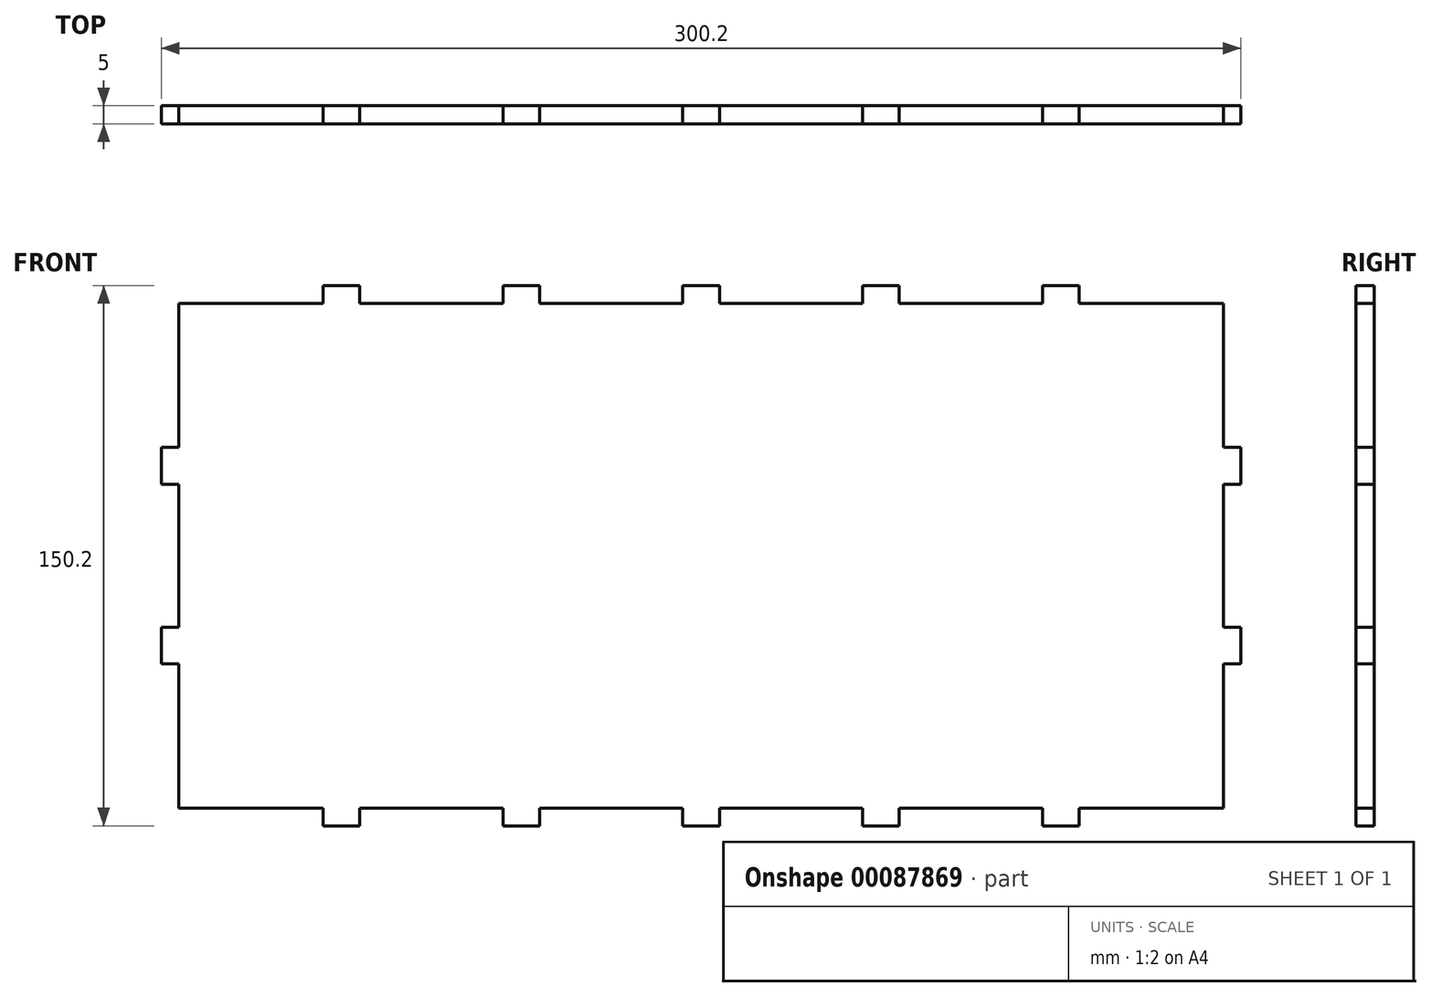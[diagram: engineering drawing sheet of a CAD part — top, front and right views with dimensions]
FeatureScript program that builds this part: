
annotation { "Feature Type Name" : "Feature", "Feature Type Description" : "" }
export const myFeature = defineFeature(function(context is Context, id is Id, definition is map)
    precondition{}
    {
        {
            var Q0;
            Q0=qCreatedBy(makeId("Front.planeOp"),FACE);
            var sketch = newSketch(context, id + "F0", { "sketchPlane" : qUnion([Q0])});
            skLineSegment(sketch, "E0.bottom", {"start": v(150.1, 75.1) * mm, "end": v(-150.1, 75.1) * mm});
            skLineSegment(sketch, "E0.top", {"start": v(150.1, -75.1) * mm, "end": v(-150.1, -75.1) * mm});
            skLineSegment(sketch, "E0.left", {"start": v(150.1, 75.1) * mm, "end": v(150.1, -75.1) * mm});
            skLineSegment(sketch, "E0.right", {"start": v(-150.1, 75.1) * mm, "end": v(-150.1, -75.1) * mm});
            skPoint(sketch, "E0.middle", {"position": v(0, 0) * mm});
            skSolve(sketch);
        }
        {
            var Q0;
            Q0=makeQuery(id+"F0.imprint","IMPRINT",FACE,{"disambiguationData":[TD([[makeQuery(id+"F0.imprint","IMPRINT",EDGE,{"derivedFrom":sQuery(id+"F0.wireOp",EDGE,"E0.bottom")}),1.0]])]});
            extrude(context, id + "F1", {"entities" : qUnion([Q0]), "depth" : 5 * mm});
        }
        {
            var Q0;
            Q0=makeQuery(id+"F1.opExtrude","CAP_FACE",FACE,{"disambiguationData":[OSD([sQuery(id+"F0.wireOp",EDGE,"E0.bottom"),sQuery(id+"F0.wireOp",EDGE,"E0.top"),sQuery(id+"F0.wireOp",EDGE,"E0.left"),sQuery(id+"F0.wireOp",EDGE,"E0.right")])],"isStart":false});
            var sketch = newSketch(context, id + "F2", { "sketchPlane" : qUnion([Q0])});
            skLineSegment(sketch, "E1.bottom", {"start": v(-150.1, 75.1) * mm, "end": v(-145.2, 75.1) * mm});
            skLineSegment(sketch, "E1.top", {"start": v(-150.1, 30.1) * mm, "end": v(-145.2, 30.1) * mm});
            skLineSegment(sketch, "E1.left", {"start": v(-150.1, 75.1) * mm, "end": v(-150.1, 30.1) * mm});
            skLineSegment(sketch, "E1.right", {"start": v(-145.2, 75.1) * mm, "end": v(-145.2, 30.1) * mm});
            skLineSegment(sketch, "E2.bottom", {"start": v(-150.1, 19.9) * mm, "end": v(-145.2, 19.9) * mm});
            skLineSegment(sketch, "E2.top", {"start": v(-150.1, -19.9) * mm, "end": v(-145.2, -19.9) * mm});
            skLineSegment(sketch, "E2.left", {"start": v(-150.1, 19.9) * mm, "end": v(-150.1, -19.9) * mm});
            skLineSegment(sketch, "E2.right", {"start": v(-145.2, 19.9) * mm, "end": v(-145.2, -19.9) * mm});
            skLineSegment(sketch, "E3.bottom", {"start": v(-150.1, -30.1) * mm, "end": v(-145.2, -30.1) * mm});
            skLineSegment(sketch, "E3.top", {"start": v(-150.1, -75.1) * mm, "end": v(-145.2, -75.1) * mm});
            skLineSegment(sketch, "E3.left", {"start": v(-150.1, -30.1) * mm, "end": v(-150.1, -75.1) * mm});
            skLineSegment(sketch, "E3.right", {"start": v(-145.2, -30.1) * mm, "end": v(-145.2, -75.1) * mm});
            skLineSegment(sketch, "E4.bottom", {"start": v(-150.1, 75.1) * mm, "end": v(-105.1, 75.1) * mm});
            skLineSegment(sketch, "E4.top", {"start": v(-150.1, 70.2) * mm, "end": v(-105.1, 70.2) * mm});
            skLineSegment(sketch, "E4.left", {"start": v(-150.1, 75.1) * mm, "end": v(-150.1, 70.2) * mm});
            skLineSegment(sketch, "E4.right", {"start": v(-105.1, 75.1) * mm, "end": v(-105.1, 70.2) * mm});
            skLineSegment(sketch, "E5.bottom", {"start": v(-94.9, 75.1) * mm, "end": v(-55.1, 75.1) * mm});
            skLineSegment(sketch, "E5.top", {"start": v(-94.9, 70.2) * mm, "end": v(-55.1, 70.2) * mm});
            skLineSegment(sketch, "E5.left", {"start": v(-94.9, 75.1) * mm, "end": v(-94.9, 70.2) * mm});
            skLineSegment(sketch, "E5.right", {"start": v(-55.1, 75.1) * mm, "end": v(-55.1, 70.2) * mm});
            skLineSegment(sketch, "E6.bottom", {"start": v(-44.9, 75.1) * mm, "end": v(-5.1, 75.1) * mm});
            skLineSegment(sketch, "E6.top", {"start": v(-44.9, 70.2) * mm, "end": v(-5.1, 70.2) * mm});
            skLineSegment(sketch, "E6.left", {"start": v(-44.9, 75.1) * mm, "end": v(-44.9, 70.2) * mm});
            skLineSegment(sketch, "E6.right", {"start": v(-5.1, 75.1) * mm, "end": v(-5.1, 70.2) * mm});
            skLineSegment(sketch, "E7.bottom", {"start": v(5.1, 75.1) * mm, "end": v(44.9, 75.1) * mm});
            skLineSegment(sketch, "E7.top", {"start": v(5.1, 70.2) * mm, "end": v(44.9, 70.2) * mm});
            skLineSegment(sketch, "E7.left", {"start": v(5.1, 75.1) * mm, "end": v(5.1, 70.2) * mm});
            skLineSegment(sketch, "E7.right", {"start": v(44.9, 75.1) * mm, "end": v(44.9, 70.2) * mm});
            skLineSegment(sketch, "E8.bottom", {"start": v(55.1, 75.1) * mm, "end": v(94.9, 75.1) * mm});
            skLineSegment(sketch, "E8.top", {"start": v(55.1, 70.2) * mm, "end": v(94.9, 70.2) * mm});
            skLineSegment(sketch, "E8.left", {"start": v(55.1, 75.1) * mm, "end": v(55.1, 70.2) * mm});
            skLineSegment(sketch, "E8.right", {"start": v(94.9, 75.1) * mm, "end": v(94.9, 70.2) * mm});
            skLineSegment(sketch, "E9.bottom", {"start": v(150.1, 75.1) * mm, "end": v(105.1, 75.1) * mm});
            skLineSegment(sketch, "E9.top", {"start": v(150.1, 70.2) * mm, "end": v(105.1, 70.2) * mm});
            skLineSegment(sketch, "E9.left", {"start": v(150.1, 75.1) * mm, "end": v(150.1, 70.2) * mm});
            skLineSegment(sketch, "E9.right", {"start": v(105.1, 75.1) * mm, "end": v(105.1, 70.2) * mm});
            skLineSegment(sketch, "E10.MirrorCS", {"start": v(-150.1, -75.1) * mm, "end": v(-150.1, -70.2) * mm});
            skLineSegment(sketch, "E11.MirrorCS", {"start": v(44.9, -75.1) * mm, "end": v(44.9, -70.2) * mm});
            skLineSegment(sketch, "E12.MirrorCS", {"start": v(-5.1, -75.1) * mm, "end": v(-5.1, -70.2) * mm});
            skLineSegment(sketch, "E13.MirrorCS", {"start": v(-55.1, -75.1) * mm, "end": v(-55.1, -70.2) * mm});
            skLineSegment(sketch, "E14.MirrorCS", {"start": v(105.1, -75.1) * mm, "end": v(105.1, -70.2) * mm});
            skLineSegment(sketch, "E15.MirrorCS", {"start": v(-105.1, -75.1) * mm, "end": v(-105.1, -70.2) * mm});
            skLineSegment(sketch, "E16.MirrorCS", {"start": v(5.1, -75.1) * mm, "end": v(5.1, -70.2) * mm});
            skLineSegment(sketch, "E17.MirrorCS", {"start": v(55.1, -75.1) * mm, "end": v(55.1, -70.2) * mm});
            skLineSegment(sketch, "E18.MirrorCS", {"start": v(-94.9, -75.1) * mm, "end": v(-94.9, -70.2) * mm});
            skLineSegment(sketch, "E19.MirrorCS", {"start": v(150.1, -75.1) * mm, "end": v(150.1, -70.2) * mm});
            skLineSegment(sketch, "E20.MirrorCS", {"start": v(94.9, -75.1) * mm, "end": v(94.9, -70.2) * mm});
            skLineSegment(sketch, "E21.MirrorCS", {"start": v(-44.9, -75.1) * mm, "end": v(-44.9, -70.2) * mm});
            skLineSegment(sketch, "E22.MirrorCS", {"start": v(55.1, -70.2) * mm, "end": v(94.9, -70.2) * mm});
            skLineSegment(sketch, "E23.MirrorCS", {"start": v(-44.9, -75.1) * mm, "end": v(-5.1, -75.1) * mm});
            skLineSegment(sketch, "E24.MirrorCS", {"start": v(150.1, -75.1) * mm, "end": v(105.1, -75.1) * mm});
            skLineSegment(sketch, "E25.MirrorCS", {"start": v(-150.1, -70.2) * mm, "end": v(-105.1, -70.2) * mm});
            skLineSegment(sketch, "E26.MirrorCS", {"start": v(-94.9, -75.1) * mm, "end": v(-55.1, -75.1) * mm});
            skLineSegment(sketch, "E27.MirrorCS", {"start": v(-94.9, -70.2) * mm, "end": v(-55.1, -70.2) * mm});
            skLineSegment(sketch, "E28.MirrorCS", {"start": v(150.1, -70.2) * mm, "end": v(105.1, -70.2) * mm});
            skLineSegment(sketch, "E29.MirrorCS", {"start": v(-44.9, -70.2) * mm, "end": v(-5.1, -70.2) * mm});
            skLineSegment(sketch, "E30.MirrorCS", {"start": v(5.1, -75.1) * mm, "end": v(44.9, -75.1) * mm});
            skLineSegment(sketch, "E31.MirrorCS", {"start": v(55.1, -75.1) * mm, "end": v(94.9, -75.1) * mm});
            skLineSegment(sketch, "E32.MirrorCS", {"start": v(-150.1, -75.1) * mm, "end": v(-105.1, -75.1) * mm});
            skLineSegment(sketch, "E33.MirrorCS", {"start": v(5.1, -70.2) * mm, "end": v(44.9, -70.2) * mm});
            skLineSegment(sketch, "E34.MirrorCS", {"start": v(150.1, -75.1) * mm, "end": v(145.2, -75.1) * mm});
            skLineSegment(sketch, "E35.MirrorCS", {"start": v(150.1, 75.1) * mm, "end": v(145.2, 75.1) * mm});
            skLineSegment(sketch, "E36.MirrorCS", {"start": v(150.1, -30.1) * mm, "end": v(145.2, -30.1) * mm});
            skLineSegment(sketch, "E37.MirrorCS", {"start": v(150.1, -19.9) * mm, "end": v(145.2, -19.9) * mm});
            skLineSegment(sketch, "E38.MirrorCS", {"start": v(150.1, 30.1) * mm, "end": v(145.2, 30.1) * mm});
            skLineSegment(sketch, "E39.MirrorCS", {"start": v(150.1, 19.9) * mm, "end": v(145.2, 19.9) * mm});
            skLineSegment(sketch, "E40.MirrorCS", {"start": v(145.2, -30.1) * mm, "end": v(145.2, -75.1) * mm});
            skLineSegment(sketch, "E41.MirrorCS", {"start": v(150.1, -30.1) * mm, "end": v(150.1, -75.1) * mm});
            skLineSegment(sketch, "E42.MirrorCS", {"start": v(145.2, 19.9) * mm, "end": v(145.2, -19.9) * mm});
            skLineSegment(sketch, "E43.MirrorCS", {"start": v(150.1, 19.9) * mm, "end": v(150.1, -19.9) * mm});
            skLineSegment(sketch, "E44.MirrorCS", {"start": v(145.2, 75.1) * mm, "end": v(145.2, 30.1) * mm});
            skLineSegment(sketch, "E45.MirrorCS", {"start": v(150.1, 75.1) * mm, "end": v(150.1, 30.1) * mm});
            skSolve(sketch);
        }
        {
            var Q0;
            Q0 = qSketchRegion(id + "F2", true);
            extrude(context, id + "F3", {"entities" : qUnion([Q0]), "operationType" : NewBodyOperationType.REMOVE, "endBound" : BoundingType.UP_TO_NEXT, "oppositeDirection" : true, "depth" : 25 * mm});
        }
    });
